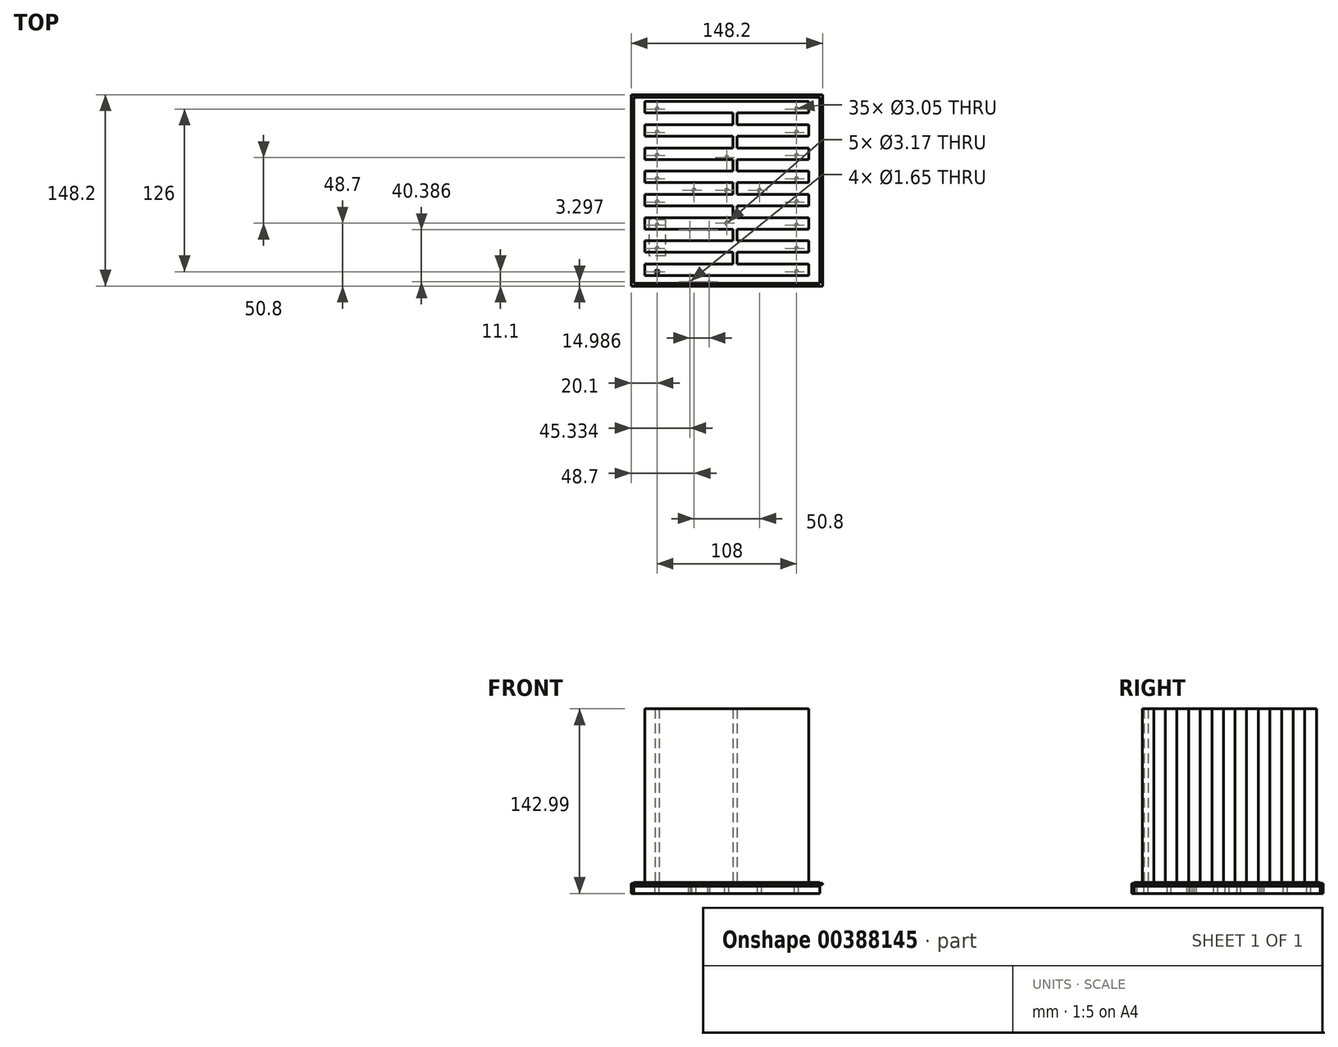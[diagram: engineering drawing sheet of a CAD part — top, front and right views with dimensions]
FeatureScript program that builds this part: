
annotation { "Feature Type Name" : "Feature", "Feature Type Description" : "" }
export const myFeature = defineFeature(function(context is Context, id is Id, definition is map)
    precondition{}
    {
        {
            assignVariable(context, id + "F0", {"name" : "hSpacer", "anyValue" : 1});
        }
        {
            assignVariable(context, id + "F1", {"name" : "tPlexi", "anyValue" : .8});
        }
        {
            assignVariable(context, id + "F2", {"name" : "hPlexi", "anyValue" : 5.9 + getVariable(context, 'hSpacer')});
        }
        {
            var Q0;
            Q0=qCreatedBy(makeId("Top.planeOp"),FACE);
            var sketch = newSketch(context, id + "F3", { "sketchPlane" : qUnion([Q0])});
            skLineSegment(sketch, "E0.bottom", {"start": v(72.07, -72.07) * mm, "end": v(-72.07, -72.07) * mm});
            skLineSegment(sketch, "E0.top", {"start": v(72.07, 72.07) * mm, "end": v(-72.07, 72.07) * mm});
            skLineSegment(sketch, "E0.left", {"start": v(72.07, -72.07) * mm, "end": v(72.07, 72.07) * mm});
            skLineSegment(sketch, "E0.right", {"start": v(-72.07, -72.07) * mm, "end": v(-72.07, 72.07) * mm});
            skSolve(sketch);
        }
        {
            var Q0;
            Q0 = qSketchRegion(id + "F3", true);
            extrude(context, id + "F4", {"entities" : qUnion([Q0]), "depth" : 1.78 * mm});
        }
        {
            var Q0;
            Q0=makeQuery(id+"F4.opExtrude","CAP_FACE",FACE,{"disambiguationData":[OSD([sQuery(id+"F3.wireOp",EDGE,"E0.bottom"),sQuery(id+"F3.wireOp",EDGE,"E0.top"),sQuery(id+"F3.wireOp",EDGE,"E0.left"),sQuery(id+"F3.wireOp",EDGE,"E0.right"),sQuery(id+"F3.wireOp",EDGE,"MW8s5i0L-Nd99-l0yK-6GKl-EVJqx4Rldbff"),sQuery(id+"F3.wireOp",EDGE,"bbdc6b1c-add9-41d6-8777-d3233f474829.0.1.0"),sQuery(id+"F3.wireOp",EDGE,"bbdc6b1c-add9-41d6-8777-d3233f474829.0.2.0"),sQuery(id+"F3.wireOp",EDGE,"bbdc6b1c-add9-41d6-8777-d3233f474829.0.3.0"),sQuery(id+"F3.wireOp",EDGE,"bbdc6b1c-add9-41d6-8777-d3233f474829.0.4.0"),sQuery(id+"F3.wireOp",EDGE,"bbdc6b1c-add9-41d6-8777-d3233f474829.0.5.0"),sQuery(id+"F3.wireOp",EDGE,"bbdc6b1c-add9-41d6-8777-d3233f474829.0.6.0"),sQuery(id+"F3.wireOp",EDGE,"bbdc6b1c-add9-41d6-8777-d3233f474829.0.7.0"),sQuery(id+"F3.wireOp",EDGE,"1edef59c-c31e-46ad-94a8-f215737e582f0.MirrorC"),sQuery(id+"F3.wireOp",EDGE,"1edef59c-c31e-46ad-94a8-f215737e582f1.MirrorC"),sQuery(id+"F3.wireOp",EDGE,"1edef59c-c31e-46ad-94a8-f215737e582f2.MirrorC"),sQuery(id+"F3.wireOp",EDGE,"1edef59c-c31e-46ad-94a8-f215737e582f3.MirrorC"),sQuery(id+"F3.wireOp",EDGE,"1edef59c-c31e-46ad-94a8-f215737e582f4.MirrorC"),sQuery(id+"F3.wireOp",EDGE,"1edef59c-c31e-46ad-94a8-f215737e582f5.MirrorC"),sQuery(id+"F3.wireOp",EDGE,"1edef59c-c31e-46ad-94a8-f215737e582f6.MirrorC"),sQuery(id+"F3.wireOp",EDGE,"1edef59c-c31e-46ad-94a8-f215737e582f7.MirrorC")])],"isStart":true});
            var sketch = newSketch(context, id + "F5", { "sketchPlane" : qUnion([Q0])});
            skLineSegment(sketch, "E1.bottom", {"start": v(-47.69, 22.81) * mm, "end": v(-60.39, 22.81) * mm});
            skLineSegment(sketch, "E1.top", {"start": v(-47.69, 50.56) * mm, "end": v(-60.39, 50.56) * mm});
            skLineSegment(sketch, "E1.left", {"start": v(-47.69, 22.81) * mm, "end": v(-47.69, 50.56) * mm});
            skLineSegment(sketch, "E1.right", {"start": v(-60.39, 22.81) * mm, "end": v(-60.39, 50.56) * mm});
            skPoint(sketch, "E1.middle", {"position": v(-54.04, 36.68) * mm});
            skSolve(sketch);
        }
        {
            var Q0;
            Q0 = qSketchRegion(id + "F5", true);
            extrude(context, id + "F6", {"entities" : qUnion([Q0]), "depth" : (getVariable(context, 'hSpacer')) * mm});
        }
        {
            var Q0;
            Q0=makeQuery(id+"F6.opExtrude","CAP_FACE",FACE,{"disambiguationData":[OSD([sQuery(id+"F5.wireOp",EDGE,"E1.bottom"),sQuery(id+"F5.wireOp",EDGE,"E1.top"),sQuery(id+"F5.wireOp",EDGE,"E1.left"),sQuery(id+"F5.wireOp",EDGE,"E1.right"),sQuery(id+"F5.wireOp",EDGE,"iTPnhCOE-9O86-hEWA-g1ar-WTCQjGTtrBPD"),sQuery(id+"F5.wireOp",EDGE,"oi7UHgfY-3mZq-2iFC-dSHU-dSUi8LMiaNtq")])],"isStart":false});
            var sketch = newSketch(context, id + "F7", { "sketchPlane" : qUnion([Q0])});
            skLineSegment(sketch, "E2.bottom", {"start": v(72.07, -72.07) * mm, "end": v(-72.07, -72.07) * mm});
            skLineSegment(sketch, "E2.top", {"start": v(72.07, 72.07) * mm, "end": v(-72.07, 72.07) * mm});
            skLineSegment(sketch, "E2.left", {"start": v(72.07, -72.07) * mm, "end": v(72.07, 72.07) * mm});
            skLineSegment(sketch, "E2.right", {"start": v(-72.07, -72.07) * mm, "end": v(-72.07, 72.07) * mm});
            skPoint(sketch, "E2.middle", {"position": v(0, 0) * mm});
            skCircle(sketch, "E3", {"center": v(0, 0) * mm, "radius": 1.59 * mm});
            skCircle(sketch, "E4", {"center": v(0, 25.4) * mm, "radius": 1.59 * mm});
            skCircle(sketch, "E5.1.0", {"center": v(-25.4, 0) * mm, "radius": 1.59 * mm});
            skCircle(sketch, "E5.2.0", {"center": v(0, -25.4) * mm, "radius": 1.59 * mm});
            skCircle(sketch, "E5.3.0", {"center": v(25.4, 0) * mm, "radius": 1.59 * mm});
            skSolve(sketch);
        }
        {
            var Q0;
            Q0 = qSketchRegion(id + "F7", true);
            extrude(context, id + "F8", {"entities" : qUnion([Q0]), "depth" : 5.6 * mm});
        }
        {
            var Q0;
            Q0=makeQuery(id+"F4.opExtrude","CAP_FACE",FACE,{"disambiguationData":[OSD([sQuery(id+"F3.wireOp",EDGE,"E0.bottom"),sQuery(id+"F3.wireOp",EDGE,"E0.top"),sQuery(id+"F3.wireOp",EDGE,"E0.left"),sQuery(id+"F3.wireOp",EDGE,"E0.right"),sQuery(id+"F3.wireOp",EDGE,"MW8s5i0L-Nd99-l0yK-6GKl-EVJqx4Rldbff"),sQuery(id+"F3.wireOp",EDGE,"bbdc6b1c-add9-41d6-8777-d3233f474829.0.1.0"),sQuery(id+"F3.wireOp",EDGE,"bbdc6b1c-add9-41d6-8777-d3233f474829.0.2.0"),sQuery(id+"F3.wireOp",EDGE,"bbdc6b1c-add9-41d6-8777-d3233f474829.0.3.0"),sQuery(id+"F3.wireOp",EDGE,"bbdc6b1c-add9-41d6-8777-d3233f474829.0.4.0"),sQuery(id+"F3.wireOp",EDGE,"bbdc6b1c-add9-41d6-8777-d3233f474829.0.5.0"),sQuery(id+"F3.wireOp",EDGE,"bbdc6b1c-add9-41d6-8777-d3233f474829.0.6.0"),sQuery(id+"F3.wireOp",EDGE,"bbdc6b1c-add9-41d6-8777-d3233f474829.0.7.0"),sQuery(id+"F3.wireOp",EDGE,"1edef59c-c31e-46ad-94a8-f215737e582f0.MirrorC"),sQuery(id+"F3.wireOp",EDGE,"1edef59c-c31e-46ad-94a8-f215737e582f1.MirrorC"),sQuery(id+"F3.wireOp",EDGE,"1edef59c-c31e-46ad-94a8-f215737e582f2.MirrorC"),sQuery(id+"F3.wireOp",EDGE,"1edef59c-c31e-46ad-94a8-f215737e582f3.MirrorC"),sQuery(id+"F3.wireOp",EDGE,"1edef59c-c31e-46ad-94a8-f215737e582f4.MirrorC"),sQuery(id+"F3.wireOp",EDGE,"1edef59c-c31e-46ad-94a8-f215737e582f5.MirrorC"),sQuery(id+"F3.wireOp",EDGE,"1edef59c-c31e-46ad-94a8-f215737e582f6.MirrorC"),sQuery(id+"F3.wireOp",EDGE,"1edef59c-c31e-46ad-94a8-f215737e582f7.MirrorC")])],"isStart":false});
            var sketch = newSketch(context, id + "F9", { "sketchPlane" : qUnion([Q0])});
            skCircle(sketch, "E6", {"center": v(-54, -63) * mm, "radius": 1.52 * mm});
            skCircle(sketch, "E7.0.1.0", {"center": v(-54, -45) * mm, "radius": 1.52 * mm});
            skCircle(sketch, "E7.0.2.0", {"center": v(-54, -27) * mm, "radius": 1.52 * mm});
            skCircle(sketch, "E7.0.3.0", {"center": v(-54, -9) * mm, "radius": 1.52 * mm});
            skCircle(sketch, "E7.0.4.0", {"center": v(-54, 9) * mm, "radius": 1.52 * mm});
            skCircle(sketch, "E7.0.5.0", {"center": v(-54, 27) * mm, "radius": 1.52 * mm});
            skCircle(sketch, "E7.0.6.0", {"center": v(-54, 45) * mm, "radius": 1.52 * mm});
            skCircle(sketch, "E7.0.7.0", {"center": v(-54, 63) * mm, "radius": 1.52 * mm});
            skLineSegment(sketch, "E7.direction1", {"start": v(-54, -63) * mm, "end": v(54, -63) * mm, "construction": true});
            skLineSegment(sketch, "E7.direction2", {"start": v(-54, -63) * mm, "end": v(-54, -45) * mm, "construction": true});
            skCircle(sketch, "E8.0.1.0", {"center": v(54, -63) * mm, "radius": 1.52 * mm});
            skCircle(sketch, "E8.0.1.1", {"center": v(54, -45) * mm, "radius": 1.52 * mm});
            skCircle(sketch, "E8.0.1.2", {"center": v(54, -27) * mm, "radius": 1.52 * mm});
            skCircle(sketch, "E8.0.1.3", {"center": v(54, -9) * mm, "radius": 1.52 * mm});
            skCircle(sketch, "E8.0.1.4", {"center": v(54, 9) * mm, "radius": 1.52 * mm});
            skCircle(sketch, "E8.0.1.5", {"center": v(54, 27) * mm, "radius": 1.52 * mm});
            skCircle(sketch, "E8.0.1.6", {"center": v(54, 45) * mm, "radius": 1.52 * mm});
            skCircle(sketch, "E8.0.1.7", {"center": v(54, 63) * mm, "radius": 1.52 * mm});
            skPoint(sketch, "E9", {"position": v(0, -63) * mm});
            skLineSegment(sketch, "E10", {"start": v(-54, 9) * mm, "end": v(-54, -9) * mm, "construction": true});
            skPoint(sketch, "E11", {"position": v(-54, 0) * mm});
            skSolve(sketch);
        }
        {
            var Q0;
            Q0 = qSketchRegion(id + "F9", true);
            extrude(context, id + "F10", {"entities" : qUnion([Q0]), "operationType" : NewBodyOperationType.REMOVE, "endBound" : BoundingType.THROUGH_ALL, "oppositeDirection" : true, "depth" : 25.4 * mm});
        }
        {
            var Q0;
            Q0=makeQuery(id+"F4.opExtrude","CAP_FACE",FACE,{"disambiguationData":[OSD([sQuery(id+"F3.wireOp",EDGE,"E0.bottom"),sQuery(id+"F3.wireOp",EDGE,"E0.top"),sQuery(id+"F3.wireOp",EDGE,"E0.left"),sQuery(id+"F3.wireOp",EDGE,"E0.right"),sQuery(id+"F3.wireOp",EDGE,"MW8s5i0L-Nd99-l0yK-6GKl-EVJqx4Rldbff"),sQuery(id+"F3.wireOp",EDGE,"bbdc6b1c-add9-41d6-8777-d3233f474829.0.1.0"),sQuery(id+"F3.wireOp",EDGE,"bbdc6b1c-add9-41d6-8777-d3233f474829.0.2.0"),sQuery(id+"F3.wireOp",EDGE,"bbdc6b1c-add9-41d6-8777-d3233f474829.0.3.0"),sQuery(id+"F3.wireOp",EDGE,"bbdc6b1c-add9-41d6-8777-d3233f474829.0.4.0"),sQuery(id+"F3.wireOp",EDGE,"bbdc6b1c-add9-41d6-8777-d3233f474829.0.5.0"),sQuery(id+"F3.wireOp",EDGE,"bbdc6b1c-add9-41d6-8777-d3233f474829.0.6.0"),sQuery(id+"F3.wireOp",EDGE,"bbdc6b1c-add9-41d6-8777-d3233f474829.0.7.0"),sQuery(id+"F3.wireOp",EDGE,"1edef59c-c31e-46ad-94a8-f215737e582f0.MirrorC"),sQuery(id+"F3.wireOp",EDGE,"1edef59c-c31e-46ad-94a8-f215737e582f1.MirrorC"),sQuery(id+"F3.wireOp",EDGE,"1edef59c-c31e-46ad-94a8-f215737e582f2.MirrorC"),sQuery(id+"F3.wireOp",EDGE,"1edef59c-c31e-46ad-94a8-f215737e582f3.MirrorC"),sQuery(id+"F3.wireOp",EDGE,"1edef59c-c31e-46ad-94a8-f215737e582f4.MirrorC"),sQuery(id+"F3.wireOp",EDGE,"1edef59c-c31e-46ad-94a8-f215737e582f5.MirrorC"),sQuery(id+"F3.wireOp",EDGE,"1edef59c-c31e-46ad-94a8-f215737e582f6.MirrorC"),sQuery(id+"F3.wireOp",EDGE,"1edef59c-c31e-46ad-94a8-f215737e582f7.MirrorC")])],"isStart":false});
            var sketch = newSketch(context, id + "F11", { "sketchPlane" : qUnion([Q0])});
            skLineSegment(sketch, "E12.bottom", {"start": v(63.5, -65.92) * mm, "end": v(-63.5, -65.92) * mm});
            skLineSegment(sketch, "E12.top", {"start": v(63.5, -57.03) * mm, "end": v(-63.5, -57.03) * mm});
            skLineSegment(sketch, "E12.left", {"start": v(63.5, -65.92) * mm, "end": v(63.5, -57.03) * mm});
            skLineSegment(sketch, "E12.right", {"start": v(-63.5, -65.92) * mm, "end": v(-63.5, -57.03) * mm});
            skPoint(sketch, "E12.middle", {"position": v(0, -61.48) * mm});
            skLineSegment(sketch, "E13", {"start": v(0, -61.48) * mm, "end": v(0, 0) * mm, "construction": true});
            skLineSegment(sketch, "E14", {"start": v(-54, -61.48) * mm, "end": v(54, -61.48) * mm, "construction": true});
            skLineSegment(sketch, "E15.0.1.0", {"start": v(-63.5, -47.92) * mm, "end": v(-63.5, -39.03) * mm});
            skPoint(sketch, "E15.0.1.1", {"position": v(0, -43.48) * mm});
            skLineSegment(sketch, "E15.0.1.2", {"start": v(63.5, -39.03) * mm, "end": v(-63.5, -39.03) * mm});
            skLineSegment(sketch, "E15.0.1.3", {"start": v(63.5, -47.92) * mm, "end": v(63.5, -39.03) * mm});
            skLineSegment(sketch, "E15.0.1.4", {"start": v(63.5, -47.92) * mm, "end": v(-63.5, -47.92) * mm});
            skLineSegment(sketch, "E15.0.2.0", {"start": v(-63.5, -29.92) * mm, "end": v(-63.5, -21.03) * mm});
            skPoint(sketch, "E15.0.2.1", {"position": v(0, -25.48) * mm});
            skLineSegment(sketch, "E15.0.2.2", {"start": v(63.5, -21.03) * mm, "end": v(-63.5, -21.03) * mm});
            skLineSegment(sketch, "E15.0.2.3", {"start": v(63.5, -29.92) * mm, "end": v(63.5, -21.03) * mm});
            skLineSegment(sketch, "E15.0.2.4", {"start": v(63.5, -29.92) * mm, "end": v(-63.5, -29.92) * mm});
            skLineSegment(sketch, "E15.0.3.0", {"start": v(-63.5, -11.92) * mm, "end": v(-63.5, -3.03) * mm});
            skPoint(sketch, "E15.0.3.1", {"position": v(0, -7.48) * mm});
            skLineSegment(sketch, "E15.0.3.2", {"start": v(63.5, -3.03) * mm, "end": v(-63.5, -3.03) * mm});
            skLineSegment(sketch, "E15.0.3.3", {"start": v(63.5, -11.92) * mm, "end": v(63.5, -3.03) * mm});
            skLineSegment(sketch, "E15.0.3.4", {"start": v(63.5, -11.92) * mm, "end": v(-63.5, -11.92) * mm});
            skLineSegment(sketch, "E15.0.4.0", {"start": v(-63.5, 6.08) * mm, "end": v(-63.5, 14.97) * mm});
            skPoint(sketch, "E15.0.4.1", {"position": v(0, 10.52) * mm});
            skLineSegment(sketch, "E15.0.4.2", {"start": v(63.5, 14.97) * mm, "end": v(-63.5, 14.97) * mm});
            skLineSegment(sketch, "E15.0.4.3", {"start": v(63.5, 6.08) * mm, "end": v(63.5, 14.97) * mm});
            skLineSegment(sketch, "E15.0.4.4", {"start": v(63.5, 6.08) * mm, "end": v(-63.5, 6.08) * mm});
            skLineSegment(sketch, "E15.0.5.0", {"start": v(-63.5, 24.08) * mm, "end": v(-63.5, 32.97) * mm});
            skPoint(sketch, "E15.0.5.1", {"position": v(0, 28.52) * mm});
            skLineSegment(sketch, "E15.0.5.2", {"start": v(63.5, 32.97) * mm, "end": v(-63.5, 32.97) * mm});
            skLineSegment(sketch, "E15.0.5.3", {"start": v(63.5, 24.08) * mm, "end": v(63.5, 32.97) * mm});
            skLineSegment(sketch, "E15.0.5.4", {"start": v(63.5, 24.08) * mm, "end": v(-63.5, 24.08) * mm});
            skLineSegment(sketch, "E15.0.6.0", {"start": v(-63.5, 42.08) * mm, "end": v(-63.5, 50.97) * mm});
            skPoint(sketch, "E15.0.6.1", {"position": v(0, 46.52) * mm});
            skLineSegment(sketch, "E15.0.6.2", {"start": v(63.5, 50.97) * mm, "end": v(-63.5, 50.97) * mm});
            skLineSegment(sketch, "E15.0.6.3", {"start": v(63.5, 42.08) * mm, "end": v(63.5, 50.97) * mm});
            skLineSegment(sketch, "E15.0.6.4", {"start": v(63.5, 42.08) * mm, "end": v(-63.5, 42.08) * mm});
            skLineSegment(sketch, "E15.0.7.0", {"start": v(-63.5, 60.08) * mm, "end": v(-63.5, 68.97) * mm});
            skPoint(sketch, "E15.0.7.1", {"position": v(0, 64.52) * mm});
            skLineSegment(sketch, "E15.0.7.2", {"start": v(63.5, 68.97) * mm, "end": v(-63.5, 68.97) * mm});
            skLineSegment(sketch, "E15.0.7.3", {"start": v(63.5, 60.08) * mm, "end": v(63.5, 68.97) * mm});
            skLineSegment(sketch, "E15.0.7.4", {"start": v(63.5, 60.08) * mm, "end": v(-63.5, 60.08) * mm});
            skLineSegment(sketch, "E15.direction1", {"start": v(-63.5, -65.92) * mm, "end": v(-38.1, -65.92) * mm, "construction": true});
            skLineSegment(sketch, "E15.direction2", {"start": v(-63.5, -65.92) * mm, "end": v(-63.5, -47.92) * mm, "construction": true});
            skLineSegment(sketch, "E16", {"start": v(4.82, -57.03) * mm, "end": v(4.82, -47.92) * mm});
            skLineSegment(sketch, "E17", {"start": v(7.8, -47.92) * mm, "end": v(7.8, -57.03) * mm});
            skLineSegment(sketch, "E18.0.1.0", {"start": v(4.82, -39.03) * mm, "end": v(4.82, -29.92) * mm});
            skLineSegment(sketch, "E18.0.1.1", {"start": v(7.8, -29.92) * mm, "end": v(7.8, -39.03) * mm});
            skLineSegment(sketch, "E18.0.2.0", {"start": v(4.82, -21.03) * mm, "end": v(4.82, -11.92) * mm});
            skLineSegment(sketch, "E18.0.2.1", {"start": v(7.8, -11.92) * mm, "end": v(7.8, -21.03) * mm});
            skLineSegment(sketch, "E18.0.3.0", {"start": v(4.82, -3.03) * mm, "end": v(4.82, 6.08) * mm});
            skLineSegment(sketch, "E18.0.3.1", {"start": v(7.8, 6.08) * mm, "end": v(7.8, -3.03) * mm});
            skLineSegment(sketch, "E18.0.4.0", {"start": v(4.82, 14.97) * mm, "end": v(4.82, 24.08) * mm});
            skLineSegment(sketch, "E18.0.4.1", {"start": v(7.8, 24.08) * mm, "end": v(7.8, 14.97) * mm});
            skLineSegment(sketch, "E18.0.5.0", {"start": v(4.82, 32.97) * mm, "end": v(4.82, 42.08) * mm});
            skLineSegment(sketch, "E18.0.5.1", {"start": v(7.8, 42.08) * mm, "end": v(7.8, 32.97) * mm});
            skLineSegment(sketch, "E18.0.6.0", {"start": v(4.82, 50.97) * mm, "end": v(4.82, 60.08) * mm});
            skLineSegment(sketch, "E18.0.6.1", {"start": v(7.8, 60.08) * mm, "end": v(7.8, 50.97) * mm});
            skLineSegment(sketch, "E18.direction1", {"start": v(4.82, -57.03) * mm, "end": v(30.22, -57.03) * mm, "construction": true});
            skLineSegment(sketch, "E18.direction2", {"start": v(4.82, -57.03) * mm, "end": v(4.82, -39.03) * mm, "construction": true});
            skCircle(sketch, "E19", {"center": v(-54, -63) * mm, "radius": 1.52 * mm});
            skSolve(sketch);
        }
        {
            var Q0;
            Q0 = qSketchRegion(id + "F11", true);
            extrude(context, id + "F12", {"entities" : qUnion([Q0]), "depth" : 134.62 * mm});
        }
        {
            var Q0;
            Q0=makeQuery(id+"F8.opExtrude","CAP_FACE",FACE,{"disambiguationData":[OSD([sQuery(id+"F7.wireOp",EDGE,"E2.bottom"),sQuery(id+"F7.wireOp",EDGE,"E2.top"),sQuery(id+"F7.wireOp",EDGE,"E2.left"),sQuery(id+"F7.wireOp",EDGE,"E2.right"),sQuery(id+"F7.wireOp",EDGE,"E3"),sQuery(id+"F7.wireOp",EDGE,"E4"),sQuery(id+"F7.wireOp",EDGE,"E5.1.0"),sQuery(id+"F7.wireOp",EDGE,"E5.2.0"),sQuery(id+"F7.wireOp",EDGE,"E5.3.0")])],"isStart":false});
            var sketch = newSketch(context, id + "F13", { "sketchPlane" : qUnion([Q0])});
            skLineSegment(sketch, "E20.bottom", {"start": v(-74.1, 74.1) * mm, "end": v(-72.07, 74.1) * mm});
            skLineSegment(sketch, "E20.top", {"start": v(-74.1, -74.1) * mm, "end": v(-72.07, -74.1) * mm});
            skLineSegment(sketch, "E20.left", {"start": v(-74.1, 74.1) * mm, "end": v(-74.1, -74.1) * mm});
            skLineSegment(sketch, "E20.right", {"start": v(-72.07, 74.1) * mm, "end": v(-72.07, -74.1) * mm});
            skSolve(sketch);
        }
        {
            var Q0;
            Q0 = qSketchRegion(id + "F13", true);
            extrude(context, id + "F14", {"entities" : qUnion([Q0]), "oppositeDirection" : true, "depth" : (getVariable(context, 'hPlexi')) * mm});
        }
        {
            var Q0;
            Q0=makeQuery(id+"F8.opExtrude","CAP_FACE",FACE,{"disambiguationData":[OSD([sQuery(id+"F7.wireOp",EDGE,"E2.bottom"),sQuery(id+"F7.wireOp",EDGE,"E2.top"),sQuery(id+"F7.wireOp",EDGE,"E2.left"),sQuery(id+"F7.wireOp",EDGE,"E2.right"),sQuery(id+"F7.wireOp",EDGE,"E3"),sQuery(id+"F7.wireOp",EDGE,"E4"),sQuery(id+"F7.wireOp",EDGE,"E5.1.0"),sQuery(id+"F7.wireOp",EDGE,"E5.2.0"),sQuery(id+"F7.wireOp",EDGE,"E5.3.0")])],"isStart":false});
            var sketch = newSketch(context, id + "F15", { "sketchPlane" : qUnion([Q0])});
            skLineSegment(sketch, "E21.bottom", {"start": v(72.07, -72.07) * mm, "end": v(-72.07, -72.07) * mm});
            skLineSegment(sketch, "E21.top", {"start": v(72.07, -74.1) * mm, "end": v(-72.07, -74.1) * mm});
            skLineSegment(sketch, "E21.left", {"start": v(72.07, -72.07) * mm, "end": v(72.07, -74.1) * mm});
            skLineSegment(sketch, "E21.right", {"start": v(-72.07, -72.07) * mm, "end": v(-72.07, -74.1) * mm});
            skSolve(sketch);
        }
        {
            var Q0;
            Q0 = qSketchRegion(id + "F15", true);
            extrude(context, id + "F16", {"entities" : qUnion([Q0]), "oppositeDirection" : true, "depth" : (getVariable(context, 'hPlexi')) * mm});
        }
        {
            var Q0;
            Q0=makeQuery(id+"F14.opExtrude","CAP_FACE",FACE,{"disambiguationData":[OSD([sQuery(id+"F13.wireOp",EDGE,"E20.bottom"),sQuery(id+"F13.wireOp",EDGE,"E20.top"),sQuery(id+"F13.wireOp",EDGE,"E20.left"),sQuery(id+"F13.wireOp",EDGE,"E20.right")])],"isStart":false});
            var sketch = newSketch(context, id + "F17", { "sketchPlane" : qUnion([Q0])});
            skLineSegment(sketch, "E22.bottom", {"start": v(-74.1, 74.1) * mm, "end": v(74.1, 74.1) * mm});
            skLineSegment(sketch, "E22.top", {"start": v(-74.1, -74.1) * mm, "end": v(74.1, -74.1) * mm});
            skLineSegment(sketch, "E22.left", {"start": v(-74.1, 74.1) * mm, "end": v(-74.1, -74.1) * mm});
            skLineSegment(sketch, "E22.right", {"start": v(74.1, 74.1) * mm, "end": v(74.1, -74.1) * mm});
            skSolve(sketch);
        }
        {
            var Q0;
            Q0 = qSketchRegion(id + "F17", true);
            extrude(context, id + "F18", {"entities" : qUnion([Q0]), "depth" : (getVariable(context, 'tPlexi')) * mm});
        }
        {
            var Q0;
            Q0=makeQuery(id+"F8.opExtrude","CAP_FACE",FACE,{"disambiguationData":[OSD([sQuery(id+"F7.wireOp",EDGE,"E2.bottom"),sQuery(id+"F7.wireOp",EDGE,"E2.top"),sQuery(id+"F7.wireOp",EDGE,"E2.left"),sQuery(id+"F7.wireOp",EDGE,"E2.right"),sQuery(id+"F7.wireOp",EDGE,"E3"),sQuery(id+"F7.wireOp",EDGE,"E4"),sQuery(id+"F7.wireOp",EDGE,"E5.1.0"),sQuery(id+"F7.wireOp",EDGE,"E5.2.0"),sQuery(id+"F7.wireOp",EDGE,"E5.3.0")])],"isStart":true});
            var sketch = newSketch(context, id + "F19", { "sketchPlane" : qUnion([Q0])});
            skLineSegment(sketch, "E23.bottom", {"start": v(-12.5, -29.15) * mm, "end": v(-30.04, -29.15) * mm, "construction": true});
            skLineSegment(sketch, "E23.top", {"start": v(-12.5, -72.07) * mm, "end": v(-30.04, -72.07) * mm, "construction": true});
            skLineSegment(sketch, "E23.left", {"start": v(-12.5, -29.15) * mm, "end": v(-12.5, -72.07) * mm, "construction": true});
            skLineSegment(sketch, "E23.right", {"start": v(-30.04, -29.15) * mm, "end": v(-30.04, -72.07) * mm, "construction": true});
            skPoint(sketch, "E23.middle", {"position": v(-21.27, -50.6) * mm});
            skCircle(sketch, "E24", {"center": v(-28.77, -30.42) * mm, "radius": 0.83 * mm, "construction": true});
            skCircle(sketch, "E25.MirrorC", {"center": v(-13.78, -30.42) * mm, "radius": 0.83 * mm, "construction": true});
            skCircle(sketch, "E26.MirrorC", {"center": v(-28.77, -70.8) * mm, "radius": 0.83 * mm, "construction": true});
            skCircle(sketch, "E27.MirrorC", {"center": v(-13.78, -70.8) * mm, "radius": 0.83 * mm, "construction": true});
            skSolve(sketch);
        }
        {
            var Q0;
            Q0=sQuery(id+"F19.wireOp",VERTEX,"E26.MirrorC.center");
            var Q1;
            Q1=sQuery(id+"F19.wireOp",VERTEX,"E27.MirrorC.center");
            var Q2;
            Q2=sQuery(id+"F19.wireOp",VERTEX,"E24.center");
            var Q3;
            Q3=sQuery(id+"F19.wireOp",VERTEX,"E25.MirrorC.center");
            var Q4;
            Q4=makeQuery(id+"F8.opExtrude","SWEPT_BODY",BODY,{"disambiguationData":[OSD([sQuery(id+"F7.wireOp",EDGE,"E2.bottom"),sQuery(id+"F7.wireOp",EDGE,"E2.top"),sQuery(id+"F7.wireOp",EDGE,"E2.left"),sQuery(id+"F7.wireOp",EDGE,"E2.right"),sQuery(id+"F7.wireOp",EDGE,"E3"),sQuery(id+"F7.wireOp",EDGE,"E4"),sQuery(id+"F7.wireOp",EDGE,"E5.1.0"),sQuery(id+"F7.wireOp",EDGE,"E5.2.0"),sQuery(id+"F7.wireOp",EDGE,"E5.3.0")])]});
            hole(context, id + "F20", {"style" : HoleStyle.SIMPLE, "endStyle" : HoleEndStyle.THROUGH, "holeDiameter" : 1.65 * mm, "isTappedThrough" : true, "tappedDepth" : 12.7 * mm, "tapClearance" : 3, "locations" : qUnion([Q0, Q1, Q2, Q3]), "scope" : qUnion([Q4])});
        }
        {
            var Q0;
            Q0=makeQuery(id+"F16.opExtrude","SWEPT_FACE",FACE,{"disambiguationData":[OSD([sQuery(id+"F15.wireOp",EDGE,"E21.bottom")])]});
            var sketch = newSketch(context, id + "F21", { "sketchPlane" : qUnion([Q0])});
            skLineSegment(sketch, "E28.bottom", {"start": v(-16.51, -24.26) * mm, "end": v(-26.04, -24.26) * mm});
            skLineSegment(sketch, "E28.top", {"start": v(-16.51, -15.37) * mm, "end": v(-26.04, -15.37) * mm});
            skLineSegment(sketch, "E28.left", {"start": v(-14.92, -22.67) * mm, "end": v(-14.92, -16.95) * mm});
            skLineSegment(sketch, "E28.right", {"start": v(-27.62, -22.67) * mm, "end": v(-27.62, -16.95) * mm});
            skPoint(sketch, "E28.middle", {"position": v(-21.27, -19.81) * mm});
            skLineSegment(sketch, "E29", {"start": v(-28.77, -25.4) * mm, "end": v(-13.78, -25.4) * mm, "construction": true});
            skLineSegment(sketch, "E30", {"start": v(-21.27, -19.81) * mm, "end": v(-21.27, -25.4) * mm, "construction": true});
            skPoint(sketch, "E31.visualSharp", {"position": v(-27.62, -15.37) * mm});
            skArc(sketch, "E31.filletArc", {"start": v(-26.04, -15.37) * mm, "mid": v(-27.16, -15.83) * mm, "end": v(-27.62, -16.95) * mm});
            skPoint(sketch, "E32.visualSharp", {"position": v(-14.92, -15.37) * mm});
            skArc(sketch, "E32.filletArc", {"start": v(-14.92, -16.95) * mm, "mid": v(-15.39, -15.83) * mm, "end": v(-16.51, -15.37) * mm});
            skPoint(sketch, "E33.visualSharp", {"position": v(-14.92, -24.26) * mm});
            skArc(sketch, "E33.filletArc", {"start": v(-16.51, -24.26) * mm, "mid": v(-15.39, -23.8) * mm, "end": v(-14.92, -22.67) * mm});
            skPoint(sketch, "E34.visualSharp", {"position": v(-27.62, -24.26) * mm});
            skArc(sketch, "E34.filletArc", {"start": v(-27.62, -22.67) * mm, "mid": v(-27.16, -23.8) * mm, "end": v(-26.04, -24.26) * mm});
            skSolve(sketch);
        }
        {
            var Q0;
            Q0 = qSketchRegion(id + "F21", true);
            extrude(context, id + "F22", {"entities" : qUnion([Q0]), "operationType" : NewBodyOperationType.REMOVE, "endBound" : BoundingType.THROUGH_ALL, "oppositeDirection" : true, "depth" : 25.4 * mm});
        }
        {
            var Q0;
            Q0=makeQuery(id+"F16.opExtrude","SWEPT_FACE",FACE,{"disambiguationData":[OSD([sQuery(id+"F15.wireOp",EDGE,"E21.top")])]});
            var sketch = newSketch(context, id + "F23", { "sketchPlane" : qUnion([Q0])});
            skCircle(sketch, "E35", {"center": v(65.72, -28.2) * mm, "radius": 1.59 * mm});
            skCircle(sketch, "E36.MirrorC", {"center": v(-65.72, -28.2) * mm, "radius": 1.59 * mm});
            skSolve(sketch);
        }
        {
            var Q0;
            Q0=sQuery(id+"F23.wireOp",VERTEX,"E36.MirrorC.center");
            var Q1;
            Q1=sQuery(id+"F23.wireOp",VERTEX,"E35.center");
            var Q2;
            Q2=makeQuery(id+"F8.opExtrude","SWEPT_BODY",BODY,{"disambiguationData":[OSD([sQuery(id+"F7.wireOp",EDGE,"E2.bottom"),sQuery(id+"F7.wireOp",EDGE,"E2.top"),sQuery(id+"F7.wireOp",EDGE,"E2.left"),sQuery(id+"F7.wireOp",EDGE,"E2.right"),sQuery(id+"F7.wireOp",EDGE,"E3"),sQuery(id+"F7.wireOp",EDGE,"E4"),sQuery(id+"F7.wireOp",EDGE,"E5.1.0"),sQuery(id+"F7.wireOp",EDGE,"E5.2.0"),sQuery(id+"F7.wireOp",EDGE,"E5.3.0"),sQuery(id+"F7.wireOp",EDGE,"wBjR8AS9-r5Bo-Mrmj-wRI2-Eno7KO10SyEJ"),sQuery(id+"F7.wireOp",EDGE,"08e8a3e5-0a2a-429a-a1f1-c252cf2d9128.1.0"),sQuery(id+"F7.wireOp",EDGE,"08e8a3e5-0a2a-429a-a1f1-c252cf2d9128.2.0"),sQuery(id+"F7.wireOp",EDGE,"08e8a3e5-0a2a-429a-a1f1-c252cf2d9128.3.0")])]});
            var Q3;
            Q3=makeQuery(id+"F16.opExtrude","SWEPT_BODY",BODY,{"disambiguationData":[OSD([sQuery(id+"F15.wireOp",EDGE,"E21.bottom"),sQuery(id+"F15.wireOp",EDGE,"E21.top"),sQuery(id+"F15.wireOp",EDGE,"E21.left"),sQuery(id+"F15.wireOp",EDGE,"E21.right")])]});
            hole(context, id + "F24", {"style" : HoleStyle.SIMPLE, "endStyle" : HoleEndStyle.BLIND, "holeDiameter" : 3.17 * mm, "holeDepth" : 12.7 * mm, "isTappedThrough" : true, "tappedDepth" : 12.7 * mm, "tapClearance" : 3, "locations" : qUnion([Q0, Q1]), "scope" : qUnion([Q2, Q3])});
        }
        {
            var Q0;
            Q0=makeQuery(id+"F14.opExtrude","SWEPT_FACE",FACE,{"disambiguationData":[OSD([sQuery(id+"F13.wireOp",EDGE,"E20.left")])]});
            var sketch = newSketch(context, id + "F25", { "sketchPlane" : qUnion([Q0])});
            skPoint(sketch, "E37", {"position": v(-53.02, -28.45) * mm});
            skPoint(sketch, "E38", {"position": v(53.02, -28.45) * mm});
            skSolve(sketch);
        }
        {
            var Q0;
            Q0=sQuery(id+"F25.wireOp",VERTEX,"E37");
            var Q1;
            Q1=sQuery(id+"F25.wireOp",VERTEX,"E38");
            var Q2;
            Q2=makeQuery(id+"F8.opExtrude","SWEPT_BODY",BODY,{"disambiguationData":[OSD([sQuery(id+"F7.wireOp",EDGE,"E2.bottom"),sQuery(id+"F7.wireOp",EDGE,"E2.top"),sQuery(id+"F7.wireOp",EDGE,"E2.left"),sQuery(id+"F7.wireOp",EDGE,"E2.right"),sQuery(id+"F7.wireOp",EDGE,"E3"),sQuery(id+"F7.wireOp",EDGE,"E4"),sQuery(id+"F7.wireOp",EDGE,"E5.1.0"),sQuery(id+"F7.wireOp",EDGE,"E5.2.0"),sQuery(id+"F7.wireOp",EDGE,"E5.3.0")])]});
            var Q3;
            Q3=makeQuery(id+"F14.opExtrude","SWEPT_BODY",BODY,{"disambiguationData":[OSD([sQuery(id+"F13.wireOp",EDGE,"E20.bottom"),sQuery(id+"F13.wireOp",EDGE,"E20.top"),sQuery(id+"F13.wireOp",EDGE,"E20.left"),sQuery(id+"F13.wireOp",EDGE,"E20.right")])]});
            hole(context, id + "F26", {"style" : HoleStyle.SIMPLE, "endStyle" : HoleEndStyle.BLIND, "holeDiameter" : 3.17 * mm, "holeDepth" : 12.7 * mm, "isTappedThrough" : true, "tappedDepth" : 12.7 * mm, "tapClearance" : 3, "locations" : qUnion([Q0, Q1]), "scope" : qUnion([Q2, Q3])});
        }
    });
